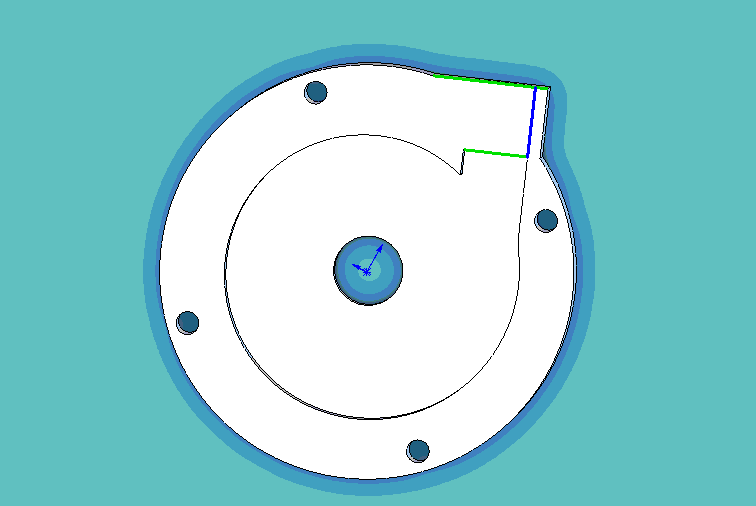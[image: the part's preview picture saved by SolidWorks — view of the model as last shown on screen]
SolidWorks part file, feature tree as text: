
SOLIDWORKS PART (.sldprt)
format: sldprt  version: not decoded by parser v0  size: 566,784 bytes
history: native  units: mm
features: sketch x7, extrude x2, cut_extrude x2, material x1, helix x1, hole x1, fillet x1 (+13 scaffold rows collapsed)
feature tree (28):
  scaffold x13  (default folders/planes/origin — collapsed)
  material  "Material <not specified>"
  sketch  "Sketch1"  dims[D1=0.0mm]
  helix  "Helix/Spiral1"  Pitch=5mm
  sketch  "Sketch3"  dims[c1.D3=~36.070819mm c1.D2=50.0mm c1.D4=50.0mm c2.D3=50.0mm c2.D2=10.0mm c3.D3=30.0mm c3.D2=18.0mm c4.D3=~15.208157mm c4.D4=25.0mm c4.D5=~13.687265mm c5.D3=15.0mm c5.D2=15.6mm c5.D4=21.6mm c5.D5=3.0mm c5.D6=~3.673503mm c6.D4=30.0mm c6.D6=~3.380416mm c7.D4=3.0mm c7.D6=~28.014445mm c8.D4=28.0mm c8.D6=~16.897538mm c8.D1=0.0mm c8.D2=15.0mm c9.D1=0.0mm c9.D4=10.0mm c10.D1=0.0mm c10.D5=3.0mm c10.D6=3.0mm]
  extrude  "Extrude1"  Depth=34mm
  cut_extrude  "Cut-Extrude2"  [1 undecoded]
  sketch  "Sketch3<6>"  dims[D1=20.0mm]
  extrude  "Extrude6"  [1 undecoded]
  sketch  "Sketch3<7>"
  hole  "M16.75 (16.75) Diameter Hole1"  Diameter=16.75mm Depth=34mm
  sketch  "Sketch21"
  sketch  "Sketch20"  dims[hole-wizard template sketch: 59 standard entries collapsed; hole parameters kept: c18.Thru Hole Dia.=16.75mm c18.Thru Hole Depth=34.0mm]
  sketch  "Sketch22"  dims[D1=13.6mm D2=8.0mm]
  cut_extrude  "Cut-Extrude3"  Depth=3mm
  fillet  "Fillet1"  Radius=3mm
decode coverage: 10 of 14 modeling features carry decoded parameters
note: ~ marks probable driven/reference dimensions
note: 2 parameter values undecoded
note: suppression state not decoded; provenance and decode notes live in map.json
